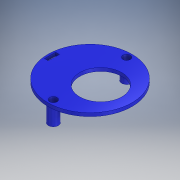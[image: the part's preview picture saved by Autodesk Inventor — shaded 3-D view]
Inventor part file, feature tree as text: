
AUTODESK INVENTOR PART (.ipt)
format: ipt  version: 2018 (Build 220112000, 112)  size: 146,944 bytes
history: native  units: mm
features: extrude x6, sketch x6, mirror x1
ambient origin geometry x8: Origin, YZ Plane, XZ Plane, XY Plane, X Axis, Y Axis, Z Axis, Center Point
bodies: Solid1 (feature_tree)
feature tree (13):
  extrude  "Extrusion1"  Depth=3.0mm TaperAngle=0.0deg
  extrude  "Extrusion2"  Depth=3.0mm TaperAngle=0.0deg
  mirror  "Mirror1"
  extrude  "Extrusion3"  Depth=9.0mm
  extrude  "Extrusion4"  Depth=15.0mm
  extrude  "Extrusion5"  Depth=18.5mm TaperAngle=0.0deg
  extrude  "Extrusion6"  Depth=10.0mm
  sketch  "Sketch1"  dims[d0=75.7mm d1=3.0mm d2=0.0mm]
  sketch  "Sketch2"  dims[d3=33.02mm d4=6.8mm d5=3.0mm d6=0.0mm]
  sketch  "Sketch3"  dims[d7=9.0mm d8=9.0mm]
  sketch  "Sketch4"  dims[d9=15.0mm d10=0.0mm d11=9.736mm]
  sketch  "Sketch5"  dims[d12=38.0mm d13=18.5mm d14=0.0mm]
  sketch  "Sketch6"  dims[d15=8.554mm d16=42.0mm d17=18.5mm d18=0.0mm d19=10.0mm d20=5.0mm d21=3.5mm d22=36.0mm d23=10.0mm d24=0.0mm]
